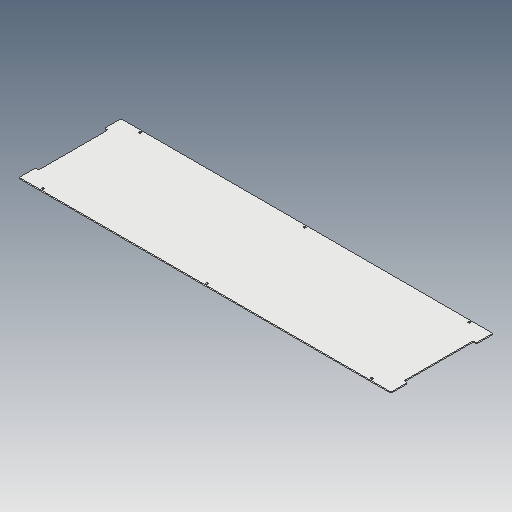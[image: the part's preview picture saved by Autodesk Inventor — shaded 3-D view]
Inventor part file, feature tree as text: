
AUTODESK INVENTOR PART (.ipt)
format: ipt  version: 2023.5 (Build 275446000, 446)  size: 101,888 bytes
history: native  units: in
note: dims shown in document units (in); Inventor stores cm internally (conversion verified against a paired STEP export)
features: fillet x1
ambient origin geometry x8: Origin, YZ Plane, XZ Plane, XY Plane, X Axis, Y Axis, Z Axis, Center Point
bodies: Solid1 (feature_tree)
feature tree (1):
  fillet  "Fillet2"  [1 undecoded]
note: 1 required parameter value undecoded (feature->parameter linkage not recoverable at this tier; creation-order binding heuristic only, values carry confidence <= 0.55)
